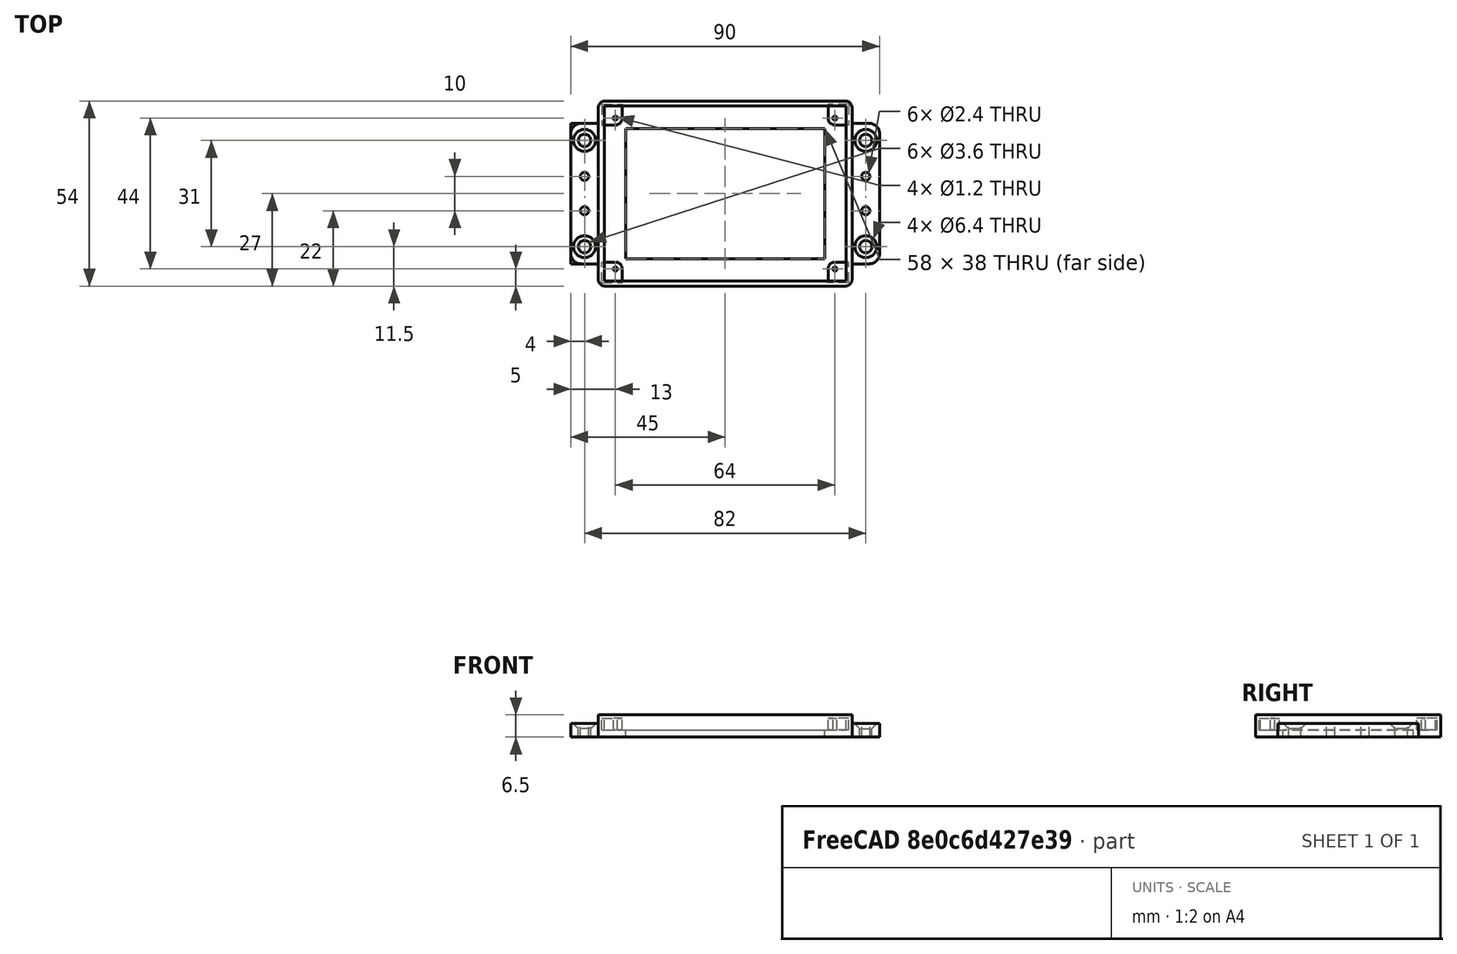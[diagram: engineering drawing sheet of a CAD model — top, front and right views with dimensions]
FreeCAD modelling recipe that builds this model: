
FCSTD DOCUMENT  (FreeCAD 0.18.4R)
Label: pcb7x5box
License: All rights reserved
LicenseURL: http://en.wikipedia.org/wiki/All_rights_reserved
objects: Part::Box×5, Part::Cylinder×3, Part::FeaturePython×3, Part::Fillet×3, Part::Cut×3, Part::Mirroring×3, Part::MultiFuse×2, Part::Compound×2, Spreadsheet::Sheet×1, App::Part×1
note: 24 computed .brp shape members not serialized (recipe doc carries the construction recipe); baked Part::Feature solids carry a one-line shape summary decoded from their .brp

FEATURE [Part::Box] Box  label="internal cube"
  AttacherType = Attacher::AttachEngine3D
  Height = 6.5
  Length = 70.4
  Placement = pos=(1.8,1.5,2) rot=(0,0,1;0rad)
  Width = 51
  expr: Placement.Base.y = p.wall - 0.5
  expr: Placement.Base.x = p.wall - 0.2
  expr: Placement.Base.z = p.wall
  expr: Height = p.wall + p.pcb_under + p.pcb_height
  expr: Width = p.pcb_width + 1
  expr: Length = p.pcb_length + 0.4
FEATURE [Spreadsheet::Sheet] Spreadsheet  label="p"
  cells = A1=pcb_length; B1(pcb_length)=70; A2=pcb_width; B2(pcb_width)=50; A3=pcb_height; B3(pcb_height)=1; A4=pcb_under; B4(pcb_under)=3.5; A5=wall; B5(wall)=2; A6=hole_dist_x; B6(hole_dist_x)=64; A7=hole_dist_y; B7(hole_dist_y)=44; A8=bottom_hole_padding; B8(bottom_hole_padding)=6; A9=attachment_hole_r; B9(attachment_hole_r)=1.8; A10=attachment_holes_dist; B10(attachment_holes_dist)=31; A11=attachment_plate_size; B11(attachment_plate_size)=41; A12=attachment_plate_width; B12(attachment_plate_width)=8; A13=attachment_plate_height; B13(attachment_plate_height)=4; A14=attachment_small_holes_dist; B14(attachment_small_holes_dist)=10; A15=attachment_small_holes_r; B15(attachment_small_holes_r)=1.2
FEATURE [Part::Box] Box001  label="external_cube"
  AttacherType = Attacher::AttachEngine3D
  Height = 6.5
  Length = 74
  Width = 54
  expr: Height = p.wall + p.pcb_under + p.pcb_height
  expr: Width = p.pcb_width + 2 * p.wall
  expr: Length = p.pcb_length + 2 * p.wall
FEATURE [Part::Cylinder] Cylinder
  Angle = 360
  AttacherType = Attacher::AttachEngine3D
  Height = 30
  Placement = pos=(5,5,-15) rot=(0,0,1;0rad)
  Radius = 0.6
  expr: Placement.Base.x = p.wall + (p.pcb_length - p.hole_dist_x) / 2
  expr: Placement.Base.y = p.wall + (p.pcb_width - p.hole_dist_y) / 2
FEATURE [Part::Box] Box002  label="hole cube"
  AttacherType = Attacher::AttachEngine3D
  Height = 3.5
  Length = 6
  Placement = pos=(1,1,2) rot=(0,0,1;0rad)
  Width = 6
  expr: Placement.Base.x = p.wall / 2
  expr: Placement.Base.y = p.wall / 2
  expr: Placement.Base.z = p.wall
  expr: Height = p.pcb_under
  expr: Width = (p.pcb_length - p.hole_dist_x) / 2 + p.wall * 1.5
  expr: Length = (p.pcb_length - p.hole_dist_x) / 2 + p.wall * 1.5
FEATURE [Part::Box] Box003  label="bottom hole cube"
  AttacherType = Attacher::AttachEngine3D
  Height = 10
  Length = 58
  Placement = pos=(8,8,-5) rot=(0,0,1;0rad)
  Width = 38
  expr: Placement.Base.y = p.wall + p.bottom_hole_padding
  expr: Placement.Base.x = p.wall + p.bottom_hole_padding
  expr: Width = p.pcb_width - 2 * p.bottom_hole_padding
  expr: Length = p.pcb_length - 2 * p.bottom_hole_padding
FEATURE [Part::MultiFuse] Fusion  label="extraction fusion"
  Shapes = -> [Box003,Box]
FEATURE [Part::Box] Box004  label="attachment plate cube"
  AttacherType = Attacher::AttachEngine3D
  Height = 4
  Length = 8
  Placement = pos=(-8,6.5,0) rot=(0,0,1;0rad)
  Width = 41
  expr: Placement.Base.y = (2 * p.wall + p.pcb_width - p.attachment_plate_size) / 2
  expr: Placement.Base.x = -p.attachment_plate_width
  expr: Height = p.attachment_plate_height
  expr: Width = p.attachment_plate_size
  expr: Length = p.attachment_plate_width
FEATURE [Part::Cylinder] Cylinder001
  Angle = 360
  AttacherType = Attacher::AttachEngine3D
  Height = 20
  Placement = pos=(-4,11.5,-5) rot=(0,0,1;0rad)
  Radius = 1.8
  expr: Placement.Base.y = (2 * p.wall + p.pcb_width - p.attachment_holes_dist) / 2
  expr: Placement.Base.x = -p.attachment_plate_width / 2
  expr: Radius = p.attachment_hole_r
FEATURE [Part::FeaturePython] Array  label="holes array"  # Draft array (typed FeaturePython)
  Angle = 360
  ArrayType = 0
  Axis = (0,0,1)
  Base = -> Cylinder001
  Center = (0,0,0)
  Fuse = false
  IntervalAxis = (0,0,0)
  IntervalX = (1,0,0)
  IntervalY = (0,31,0)
  IntervalZ = (0,0,1)
  NumberPolar = 1
  NumberX = 1
  NumberY = 2
  NumberZ = 1
  expr: IntervalY.y = p.attachment_holes_dist
FEATURE [Part::Fillet] Fillet001
  Base = -> Box002
  Edges = 1 edges r=2: [Edge7]
FEATURE [Part::Cut] Cut001
  Base = -> Fillet001
  Tool = -> Cylinder
FEATURE [Part::Mirroring] Part__Mirroring  label="Cut001 (Mirror #1)"
  Base = (0,0,0)
  Normal = (1,0,0)
  Placement = pos=(74,0,0) rot=(0,0,1;0rad)
  Source = -> Cut001
  expr: Placement.Base.x = 2 * p.wall + p.pcb_length
FEATURE [Part::Compound] Compound
  Links = -> [Part__Mirroring,Cut001]
FEATURE [Part::Mirroring] Part__Mirroring001  label="Compound (Mirror #2)"
  Base = (0,0,0)
  Normal = (0,1,0)
  Placement = pos=(0,54,0) rot=(0,0,1;0rad)
  Source = -> Compound
  expr: Placement.Base.y = 2 * p.wall + p.pcb_width
FEATURE [Part::Fillet] Fillet002  label="external cube fillet"
  Base = -> Box001
  Edges = 4 edges r=2: [Edge1,Edge3,Edge5,Edge7]
FEATURE [Part::Cut] Cut  label="main cube cut"
  Base = -> Fillet002
  Tool = -> Fusion
FEATURE [Part::Cylinder] Cylinder002
  Angle = 360
  AttacherType = Attacher::AttachEngine3D
  Height = 20
  Placement = pos=(-4,22,-5) rot=(0,0,1;0rad)
  Radius = 1.2
  expr: Radius = p.attachment_small_holes_r
  expr: Placement.Base.y = (2 * p.wall + p.pcb_width - p.attachment_small_holes_dist) / 2
  expr: Placement.Base.x = -p.attachment_plate_width / 2
FEATURE [Part::FeaturePython] Array001  label="small holes array"  # Draft array (typed FeaturePython)
  Angle = 360
  ArrayType = 0
  Axis = (0,0,1)
  Base = -> Cylinder002
  Center = (0,0,0)
  Fuse = false
  IntervalAxis = (0,0,0)
  IntervalX = (1,0,0)
  IntervalY = (0,10,0)
  IntervalZ = (0,0,1)
  NumberPolar = 1
  NumberX = 1
  NumberY = 2
  NumberZ = 1
  expr: IntervalY.y = p.attachment_small_holes_dist
FEATURE [Part::MultiFuse] Fusion001
  Shapes = -> [Array,Array001]
FEATURE [Part::Cut] Cut002
  Base = -> Box004
  Tool = -> Fusion001
FEATURE [Part::FeaturePython] Countersunk  # WARN: FeaturePython — macro-defined, semantics opaque (R4)
  baseObject = -> Cut002
  diameters = Edge10:M3:0:0:Default | Edge13:M3:0:0:Default
FEATURE [Part::Fillet] Fillet  label="attachment plate fillet"
  Base = -> Countersunk
  Edges = 2 edges r=3: [Edge1,Edge3]
FEATURE [Part::Mirroring] Part__Mirroring002  label="attachment plate fillet (Mirror #3)"
  Base = (0,0,0)
  Normal = (1,0,0)
  Placement = pos=(74,0,0) rot=(0,0,1;0rad)
  Source = -> Fillet
  expr: Placement.Base.x = 2 * p.wall + p.pcb_length
FEATURE [Part::Compound] Compound001  label="7x5pcb box compound"
  Links = -> [Cut,Compound,Part__Mirroring001,Fillet,Part__Mirroring002]
FEATURE [App::Part] Part  label="7x5pcb box part"
  Group = -> [Box,Box001,Cut,Cylinder,Box002,Cut001,Part__Mirroring,Compound,Part__Mirroring001,Box003,Fusion,Compound001,Box004,Cylinder001,Array,Cut002,Fillet,Fillet001,Part__Mirroring002,Fillet002,Fusion001,Cylinder002,Array001,Countersunk]
  Origin = -> Origin
